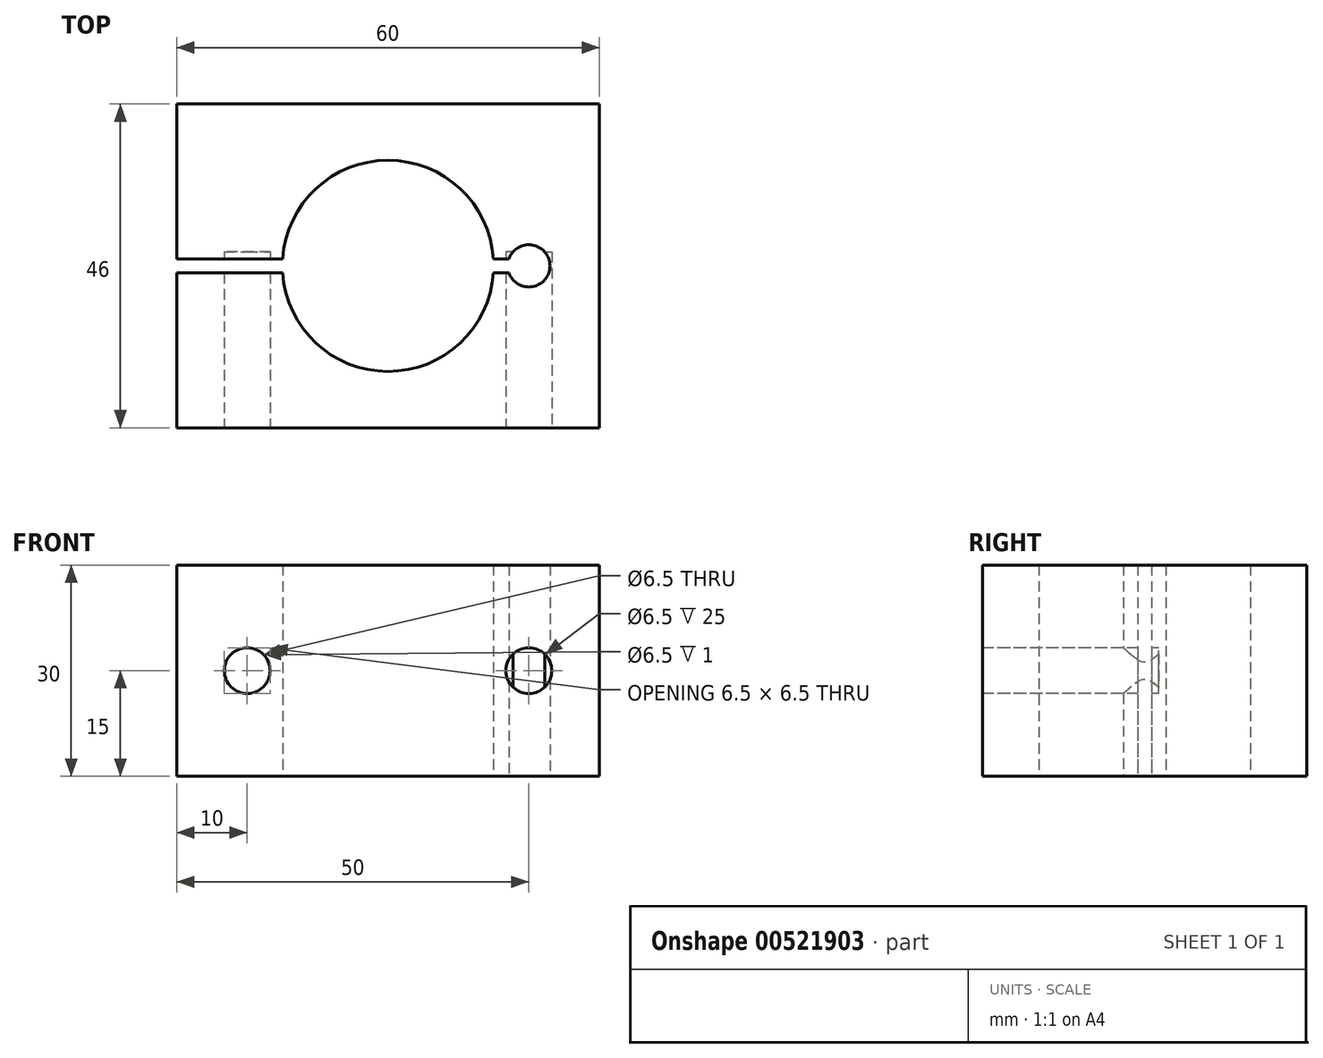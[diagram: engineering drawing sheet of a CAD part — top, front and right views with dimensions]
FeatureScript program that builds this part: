
annotation { "Feature Type Name" : "Feature", "Feature Type Description" : "" }
export const myFeature = defineFeature(function(context is Context, id is Id, definition is map)
    precondition{}
    {
        {
            var Q0;
            Q0=qCreatedBy(makeId("Top.planeOp"),FACE);
            var sketch = newSketch(context, id + "F0", { "sketchPlane" : qUnion([Q0])});
            skLineSegment(sketch, "E0.bottom", {"start": v(-30, -23) * mm, "end": v(30, -23) * mm});
            skLineSegment(sketch, "E0.top", {"start": v(-30, 23) * mm, "end": v(30, 23) * mm});
            skLineSegment(sketch, "E0.right", {"start": v(30, -23) * mm, "end": v(30, 23) * mm});
            skArc(sketch, "E1", {"start": v(-14.97, -1) * mm, "mid": v(0, -15) * mm, "end": v(14.97, -1) * mm});
            skLineSegment(sketch, "E2", {"start": v(-30, 23) * mm, "end": v(-30, 1) * mm});
            skLineSegment(sketch, "E3", {"start": v(-30, -23) * mm, "end": v(-30, -1) * mm});
            skLineSegment(sketch, "E4", {"start": v(-30, 1) * mm, "end": v(-14.97, 1) * mm});
            skLineSegment(sketch, "E5", {"start": v(-30, -1) * mm, "end": v(-14.97, -1) * mm});
            skArc(sketch, "E6", {"start": v(17.17, -1) * mm, "mid": v(23, 0) * mm, "end": v(17.17, 1) * mm});
            skLineSegment(sketch, "E7", {"start": v(17.17, 1) * mm, "end": v(14.97, 1) * mm});
            skLineSegment(sketch, "E8", {"start": v(17.17, -1) * mm, "end": v(14.97, -1) * mm});
            skLineSegment(sketch, "E9", {"start": v(16.07, 1) * mm, "end": v(-14.97, 1) * mm, "construction": true});
            skLineSegment(sketch, "E10", {"start": v(-14.97, -1) * mm, "end": v(14.97, -1) * mm, "construction": true});
            skArc(sketch, "E11.trimOffspring", {"start": v(14.97, 1) * mm, "mid": v(0, 15) * mm, "end": v(-14.97, 1) * mm});
            skSolve(sketch);
        }
        {
            var Q0;
            Q0 = qSketchRegion(id + "F0", true);
            extrude(context, id + "F1", {"entities" : qUnion([Q0]), "depth" : 30 * mm, "offsetDistance" : 25 * mm});
        }
        {
            var Q0;
            Q0=makeQuery(id+"F1.opExtrude","SWEPT_FACE",FACE,{"disambiguationData":[OSD([sQuery(id+"F0.wireOp",EDGE,"E0.bottom")])]});
            var sketch = newSketch(context, id + "F2", { "sketchPlane" : qUnion([Q0])});
            skCircle(sketch, "E12", {"center": v(-20, 15) * mm, "radius": 3.25 * mm});
            skPoint(sketch, "E12.centerSnap0", {"position": v(-30, 15) * mm});
            skCircle(sketch, "E13", {"center": v(20, 15) * mm, "radius": 3.25 * mm});
            skPoint(sketch, "E13.centerSnap0", {"position": v(30, 15) * mm});
            skSolve(sketch);
        }
        {
            var Q0;
            Q0 = qSketchRegion(id + "F2", true);
            extrude(context, id + "F3", {"entities" : qUnion([Q0]), "operationType" : NewBodyOperationType.REMOVE, "oppositeDirection" : true, "depth" : 25 * mm, "offsetDistance" : 25 * mm});
        }
    });
